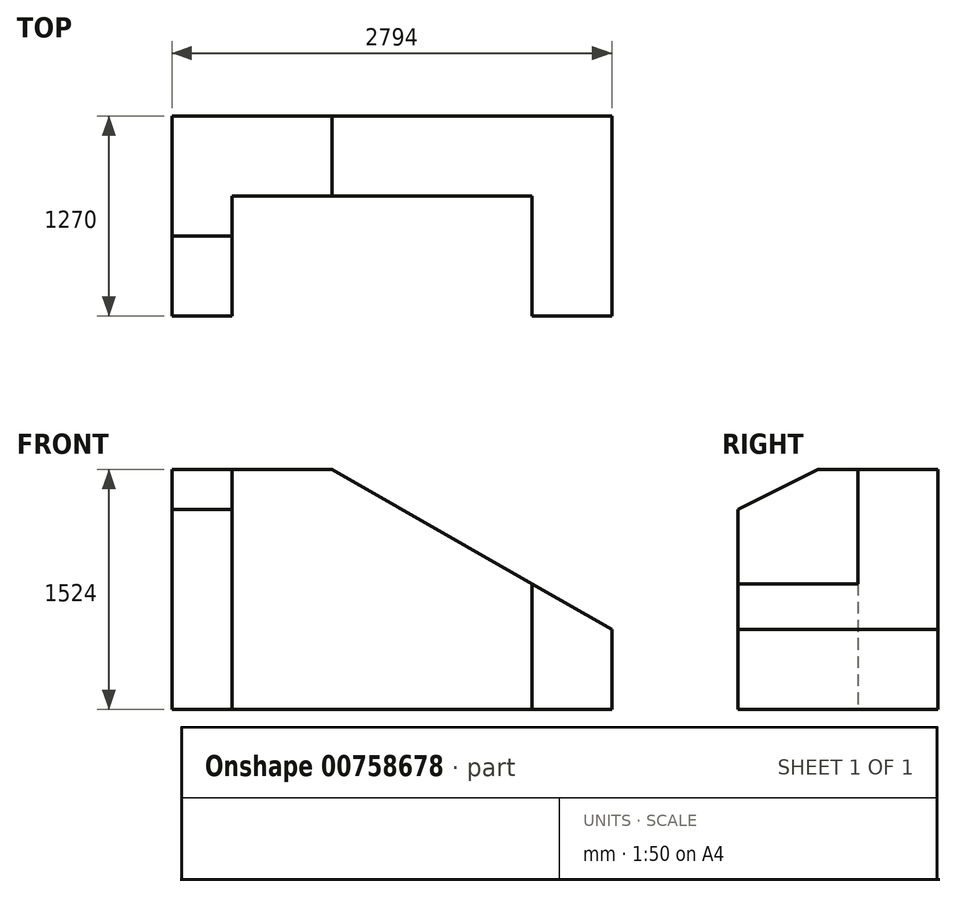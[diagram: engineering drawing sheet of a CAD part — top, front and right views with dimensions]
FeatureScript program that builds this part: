
annotation { "Feature Type Name" : "Feature", "Feature Type Description" : "" }
export const myFeature = defineFeature(function(context is Context, id is Id, definition is map)
    precondition{}
    {
        {
            var Q0;
            Q0=qCreatedBy(makeId("Front.planeOp"),FACE);
            var sketch = newSketch(context, id + "F0", { "sketchPlane" : qUnion([Q0])});
            skLineSegment(sketch, "E0.bottom", {"start": v(0, 0) * mm, "end": v(2794, 0) * mm});
            skLineSegment(sketch, "E0.top", {"start": v(0, 1524) * mm, "end": v(2794, 1524) * mm});
            skLineSegment(sketch, "E0.left", {"start": v(0, 0) * mm, "end": v(0, 1524) * mm});
            skLineSegment(sketch, "E0.right", {"start": v(2794, 0) * mm, "end": v(2794, 1524) * mm});
            skSolve(sketch);
        }
        {
            var Q0;
            Q0=makeQuery(id+"F0.imprint","IMPRINT",FACE,{"disambiguationData":[TD([[makeQuery(id+"F0.imprint","IMPRINT",EDGE,{"derivedFrom":sQuery(id+"F0.wireOp",EDGE,"E0.bottom")}),1.0]])]});
            extrude(context, id + "F1", {"entities" : qUnion([Q0]), "depth" : 1270 * mm, "offsetDistance" : 25.4 * mm});
        }
        {
            var Q0;
            Q0=makeQuery(id+"F1.opExtrude","CAP_FACE",FACE,{"disambiguationData":[OSD([sQuery(id+"F0.wireOp",EDGE,"E0.bottom"),sQuery(id+"F0.wireOp",EDGE,"E0.top"),sQuery(id+"F0.wireOp",EDGE,"E0.left"),sQuery(id+"F0.wireOp",EDGE,"E0.right")])],"isStart":false});
            var sketch = newSketch(context, id + "F2", { "sketchPlane" : qUnion([Q0])});
            skLineSegment(sketch, "E1", {"start": v(0, 1524) * mm, "end": v(381, 1524) * mm});
            skLineSegment(sketch, "E2", {"start": v(381, 1524) * mm, "end": v(381, 0) * mm});
            skLineSegment(sketch, "E3", {"start": v(381, 0) * mm, "end": v(0, 0) * mm});
            skLineSegment(sketch, "E4", {"start": v(0, 0) * mm, "end": v(0, 1524) * mm});
            skLineSegment(sketch, "E5", {"start": v(2794, 1524) * mm, "end": v(2286, 1524) * mm});
            skLineSegment(sketch, "E6", {"start": v(2286, 1524) * mm, "end": v(2286, 0) * mm});
            skLineSegment(sketch, "E7", {"start": v(2286, 0) * mm, "end": v(2794, 0) * mm});
            skSolve(sketch);
        }
        {
            var Q0;
            {var subQ0=sQuery(id+"F2.wireOp",EDGE,"E2");Q0=makeQuery(id+"F2.imprint","IMPRINT",FACE,{"disambiguationData":[TD([[makeQuery(id+"F2.imprint","IMPRINT",EDGE,{"derivedFrom":subQ0}),1.0]])]});}
            extrude(context, id + "F3", {"entities" : qUnion([Q0]), "operationType" : NewBodyOperationType.REMOVE, "oppositeDirection" : true, "depth" : 762 * mm, "offsetDistance" : 25.4 * mm});
        }
        {
            var Q0;
            Q0=makeQuery(id+"F1.opExtrude","SWEPT_FACE",FACE,{"disambiguationData":[OSD([sQuery(id+"F0.wireOp",EDGE,"E0.left")])]});
            var sketch = newSketch(context, id + "F4", { "sketchPlane" : qUnion([Q0])});
            skLineSegment(sketch, "E8", {"start": v(0, 1524) * mm, "end": v(762, 1524) * mm});
            skLineSegment(sketch, "E9", {"start": v(762, 1524) * mm, "end": v(1270, 1270) * mm});
            skLineSegment(sketch, "E10", {"start": v(1270, 1270) * mm, "end": v(1270, 0) * mm});
            skSolve(sketch);
        }
        {
            var Q0;
            {var subQ0=sQuery(id+"F4.wireOp",EDGE,"E9");Q0=makeQuery(id+"F4.imprint","IMPRINT",FACE,{"disambiguationData":[TD([[makeQuery(id+"F4.imprint","IMPRINT",EDGE,{"derivedFrom":subQ0}),1.0]])]});}
            extrude(context, id + "F5", {"entities" : qUnion([Q0]), "operationType" : NewBodyOperationType.REMOVE, "oppositeDirection" : true, "depth" : 381 * mm, "offsetDistance" : 25.4 * mm});
        }
        {
            var Q0;
            Q0=makeQuery(id+"F1.opExtrude","CAP_FACE",FACE,{"disambiguationData":[OSD([sQuery(id+"F0.wireOp",EDGE,"E0.bottom"),sQuery(id+"F0.wireOp",EDGE,"E0.top"),sQuery(id+"F0.wireOp",EDGE,"E0.left"),sQuery(id+"F0.wireOp",EDGE,"E0.right")])],"isStart":true});
            var sketch = newSketch(context, id + "F6", { "sketchPlane" : qUnion([Q0])});
            skLineSegment(sketch, "E11", {"start": v(0, 1524) * mm, "end": v(-1016, 1524) * mm});
            skLineSegment(sketch, "E12", {"start": v(-1016, 1524) * mm, "end": v(-2794, 508) * mm});
            skLineSegment(sketch, "E13", {"start": v(-2794, 508) * mm, "end": v(-2794, 0) * mm});
            skSolve(sketch);
        }
        {
            var Q0;
            {var subQ0=sQuery(id+"F6.wireOp",EDGE,"E12");Q0=makeQuery(id+"F6.imprint","IMPRINT",FACE,{"disambiguationData":[TD([[makeQuery(id+"F6.imprint","IMPRINT",EDGE,{"derivedFrom":subQ0}),-1.0]])]});}
            extrude(context, id + "F7", {"entities" : qUnion([Q0]), "operationType" : NewBodyOperationType.REMOVE, "oppositeDirection" : true, "depth" : 1270 * mm, "offsetDistance" : 25.4 * mm});
        }
    });
